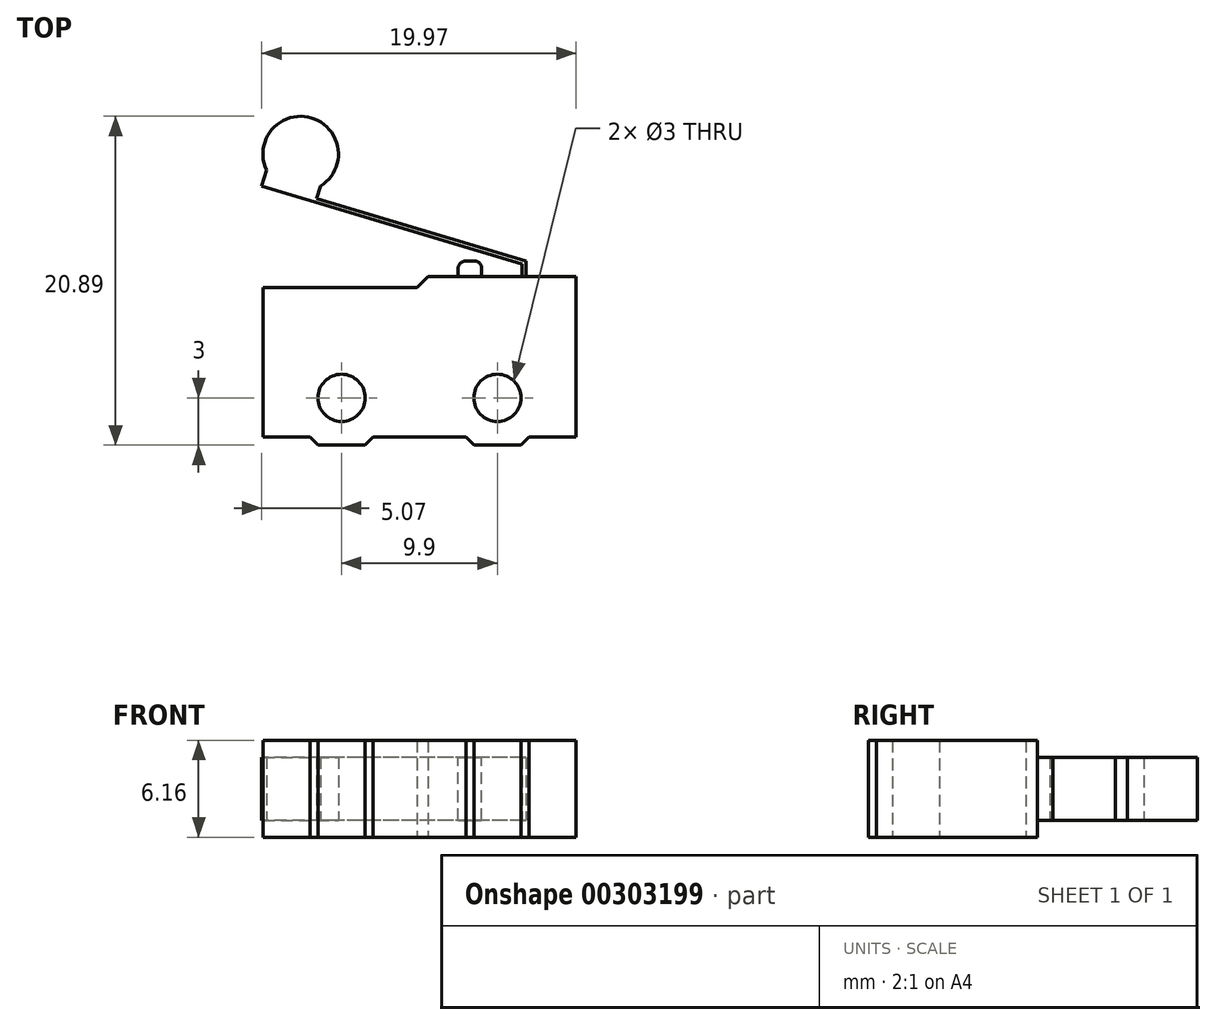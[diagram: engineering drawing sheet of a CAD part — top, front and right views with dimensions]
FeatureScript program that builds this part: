
annotation { "Feature Type Name" : "Feature", "Feature Type Description" : "" }
export const myFeature = defineFeature(function(context is Context, id is Id, definition is map)
    precondition{}
    {
        {
            var Q0;
            Q0=qCreatedBy(makeId("Top.planeOp"),FACE);
            var sketch = newSketch(context, id + "F0", { "sketchPlane" : qUnion([Q0])});
            skLineSegment(sketch, "E0.bottom", {"start": v(9.95, -5.35) * mm, "end": v(-9.95, -5.35) * mm});
            skLineSegment(sketch, "E0.top", {"start": v(9.95, 5.35) * mm, "end": v(-9.95, 5.35) * mm});
            skLineSegment(sketch, "E0.left", {"start": v(9.95, -5.35) * mm, "end": v(9.95, 5.35) * mm});
            skLineSegment(sketch, "E0.right", {"start": v(-9.95, -5.35) * mm, "end": v(-9.95, 5.35) * mm});
            skPoint(sketch, "E0.middle", {"position": v(0, 0) * mm});
            skSolve(sketch);
        }
        {
            var Q0;
            Q0=qSketchRegion(id+"F0",true);
            extrude(context, id + "F1", {"entities" : qUnion([Q0]), "depth" : (6.15 / 2) * mm, "hasSecondDirection" : true, "secondDirectionOppositeDirection" : true, "secondDirectionDepth" : (6.15 / 2) * mm});
        }
        {
            var Q0;
            Q0=makeQuery(id+"F1.opExtrude","SWEPT_FACE",FACE,{"disambiguationData":[OSD([sQuery(id+"F0.wireOp",EDGE,"E0.top")])]});
            var sketch = newSketch(context, id + "F2", { "sketchPlane" : qUnion([Q0])});
            skLineSegment(sketch, "E1.bottom", {"start": v(-2.45, -2) * mm, "end": v(-3.95, -2) * mm});
            skLineSegment(sketch, "E1.top", {"start": v(-2.45, 2) * mm, "end": v(-3.95, 2) * mm});
            skLineSegment(sketch, "E1.left", {"start": v(-2.45, -2) * mm, "end": v(-2.45, 2) * mm});
            skLineSegment(sketch, "E1.right", {"start": v(-3.95, -2) * mm, "end": v(-3.95, 2) * mm});
            skPoint(sketch, "E1.middle", {"position": v(-3.2, 0) * mm});
            skSolve(sketch);
        }
        {
            var Q0;
            Q0=qSketchRegion(id+"F2",true);
            extrude(context, id + "F3", {"entities" : qUnion([Q0]), "operationType" : NewBodyOperationType.ADD, "depth" : 1 * mm});
        }
        {
            var Q0;
            Q0=makeQuery(id+"F3.opExtrude","CAP_EDGE",EDGE,{"disambiguationData":[OSD([sQuery(id+"F2.wireOp",EDGE,"E1.left")])],"isStart":false});
            var Q1;
            Q1=makeQuery(id+"F3.opExtrude","CAP_EDGE",EDGE,{"disambiguationData":[OSD([sQuery(id+"F2.wireOp",EDGE,"E1.right")])],"isStart":false});
            fillet(context, id + "F4", {"entities" : qUnion([Q0, Q1]), "radius" : 0.5 * mm, "tangentPropagation" : true, "allowEdgeOverflow" : false});
        }
        {
            var Q0;
            Q0=makeQuery(id+"F3.opExtrude","SWEPT_FACE",FACE,{"disambiguationData":[OSD([sQuery(id+"F2.wireOp",EDGE,"E1.bottom")])]});
            var sketch = newSketch(context, id + "F5", { "sketchPlane" : qUnion([Q0])});
            skLineSegment(sketch, "E2.0", {"start": v(9.95, -5.35) * mm, "end": v(-9.95, -5.35) * mm, "construction": true});
            skLineSegment(sketch, "E3", {"start": v(6.75, -5.35) * mm, "end": v(6.75, -6.35) * mm});
            skLineSegment(sketch, "E4", {"start": v(-9.95, -5.35) * mm, "end": v(-9.95, -11.35) * mm, "construction": true});
            skLineSegment(sketch, "E5", {"start": v(6.75, -6.35) * mm, "end": v(-6.53, -10.33) * mm});
            skLineSegment(sketch, "E6", {"start": v(-9.95, -11.35) * mm, "end": v(-9.95, -19.7) * mm, "construction": true});
            skArc(sketch, "E7", {"start": v(-9.72, -12.11) * mm, "mid": v(-6.86, -15.44) * mm, "end": v(-6.3, -11.09) * mm});
            skLineSegment(sketch, "E8", {"start": v(-8.24, -10.84) * mm, "end": v(-6.71, -15.94) * mm, "construction": true});
            skLineSegment(sketch, "E9", {"start": v(-9.95, -11.35) * mm, "end": v(-9.72, -12.11) * mm});
            skLineSegment(sketch, "E10", {"start": v(-6.53, -10.33) * mm, "end": v(-6.3, -11.09) * mm});
            skLineSegment(sketch, "E11.0", {"start": v(6.5, -5.35) * mm, "end": v(6.5, -6.16) * mm});
            skLineSegment(sketch, "E12", {"start": v(6.5, -6.16) * mm, "end": v(-9.95, -11.09) * mm});
            skLineSegment(sketch, "E13", {"start": v(-9.95, -11.35) * mm, "end": v(-10.02, -11.11) * mm});
            skLineSegment(sketch, "E14", {"start": v(-10.02, -11.11) * mm, "end": v(-9.95, -11.09) * mm});
            skLineSegment(sketch, "E15", {"start": v(6.5, -5.35) * mm, "end": v(6.75, -5.35) * mm});
            skSolve(sketch);
        }
        {
            var Q0;
            Q0=qSketchRegion(id+"F5",true);
            extrude(context, id + "F6", {"entities" : qUnion([Q0]), "operationType" : NewBodyOperationType.ADD, "oppositeDirection" : true, "depth" : 4 * mm});
        }
        {
            var Q0;
            Q0=makeQuery(id+"F1.opExtrude","CAP_FACE",FACE,{"disambiguationData":[OSD([sQuery(id+"F0.wireOp",EDGE,"E0.bottom"),sQuery(id+"F0.wireOp",EDGE,"E0.top"),sQuery(id+"F0.wireOp",EDGE,"E0.left"),sQuery(id+"F0.wireOp",EDGE,"E0.right")])],"isStart":true});
            var sketch = newSketch(context, id + "F7", { "sketchPlane" : qUnion([Q0])});
            skLineSegment(sketch, "E16.bottom", {"start": v(-9.95, -5.35) * mm, "end": v(0.55, -5.35) * mm});
            skLineSegment(sketch, "E16.top", {"start": v(-9.95, -4.65) * mm, "end": v(0.55, -4.65) * mm});
            skLineSegment(sketch, "E16.left", {"start": v(-9.95, -5.35) * mm, "end": v(-9.95, -4.65) * mm});
            skLineSegment(sketch, "E16.right", {"start": v(0.55, -5.35) * mm, "end": v(0.55, -4.65) * mm});
            skLineSegment(sketch, "E17.bottom", {"start": v(-9.95, 5.35) * mm, "end": v(-6.45, 5.35) * mm});
            skLineSegment(sketch, "E17.top", {"start": v(-9.95, 4.85) * mm, "end": v(-6.45, 4.85) * mm});
            skLineSegment(sketch, "E17.left", {"start": v(-9.95, 5.35) * mm, "end": v(-9.95, 4.85) * mm});
            skLineSegment(sketch, "E17.right", {"start": v(-6.45, 5.35) * mm, "end": v(-6.45, 4.85) * mm});
            skLineSegment(sketch, "E18.MirrorCS", {"start": v(9.95, 5.35) * mm, "end": v(9.95, 4.85) * mm});
            skLineSegment(sketch, "E19.MirrorCS", {"start": v(6.45, 5.35) * mm, "end": v(6.45, 4.85) * mm});
            skLineSegment(sketch, "E20.MirrorCS", {"start": v(9.95, 4.85) * mm, "end": v(6.45, 4.85) * mm});
            skLineSegment(sketch, "E21.MirrorCS", {"start": v(9.95, 5.35) * mm, "end": v(6.45, 5.35) * mm});
            skLineSegment(sketch, "E22.bottom", {"start": v(-3.45, 5.35) * mm, "end": v(3.45, 5.35) * mm});
            skLineSegment(sketch, "E22.top", {"start": v(-3.45, 4.85) * mm, "end": v(3.45, 4.85) * mm});
            skLineSegment(sketch, "E22.left", {"start": v(-3.45, 5.35) * mm, "end": v(-3.45, 4.85) * mm});
            skLineSegment(sketch, "E22.right", {"start": v(3.45, 5.35) * mm, "end": v(3.45, 4.85) * mm});
            skCircle(sketch, "E23", {"center": v(4.95, 2.35) * mm, "radius": 1.5 * mm});
            skCircle(sketch, "E24", {"center": v(-4.95, 2.35) * mm, "radius": 1.5 * mm});
            skSolve(sketch);
        }
        {
            var Q0;
            Q0=qSketchRegion(id+"F7",true);
            extrude(context, id + "F8", {"entities" : qUnion([Q0]), "operationType" : NewBodyOperationType.REMOVE, "oppositeDirection" : true, "depth" : 25 * mm});
        }
        {
            var Q0;
            Q0=makeQuery(id+"F8.boolean.opBoolean","COPY",EDGE,{"derivedFrom":makeQuery(id+"F8.opExtrude","SWEPT_EDGE",EDGE,{"disambiguationData":[OSD([sQuery(id+"F7.wireOp",EDGE,"E16.top"),sQuery(id+"F7.wireOp",EDGE,"E16.right")])]})});
            chamfer(context, id + "F9", {"entities" : qUnion([Q0]), "width" : 0.7 * mm, "tangentPropagation" : true});
        }
        {
            var Q0;
            Q0=makeQuery(id+"F8.boolean.opBoolean","COPY",EDGE,{"derivedFrom":makeQuery(id+"F8.opExtrude","SWEPT_EDGE",EDGE,{"disambiguationData":[OSD([sQuery(id+"F7.wireOp",EDGE,"E19.MirrorCS"),sQuery(id+"F7.wireOp",EDGE,"E20.MirrorCS")])]})});
            var Q1;
            Q1=makeQuery(id+"F8.boolean.opBoolean","COPY",EDGE,{"derivedFrom":makeQuery(id+"F8.opExtrude","SWEPT_EDGE",EDGE,{"disambiguationData":[OSD([sQuery(id+"F7.wireOp",EDGE,"E22.top"),sQuery(id+"F7.wireOp",EDGE,"E22.right")])]})});
            var Q2;
            Q2=makeQuery(id+"F8.boolean.opBoolean","COPY",EDGE,{"derivedFrom":makeQuery(id+"F8.opExtrude","SWEPT_EDGE",EDGE,{"disambiguationData":[OSD([sQuery(id+"F7.wireOp",EDGE,"E22.top"),sQuery(id+"F7.wireOp",EDGE,"E22.left")])]})});
            var Q3;
            Q3=makeQuery(id+"F8.boolean.opBoolean","COPY",EDGE,{"derivedFrom":makeQuery(id+"F8.opExtrude","SWEPT_EDGE",EDGE,{"disambiguationData":[OSD([sQuery(id+"F7.wireOp",EDGE,"E17.top"),sQuery(id+"F7.wireOp",EDGE,"E17.right")])]})});
            chamfer(context, id + "F10", {"entities" : qUnion([Q0, Q1, Q2, Q3]), "width" : 0.5 * mm, "tangentPropagation" : true});
        }
    });
